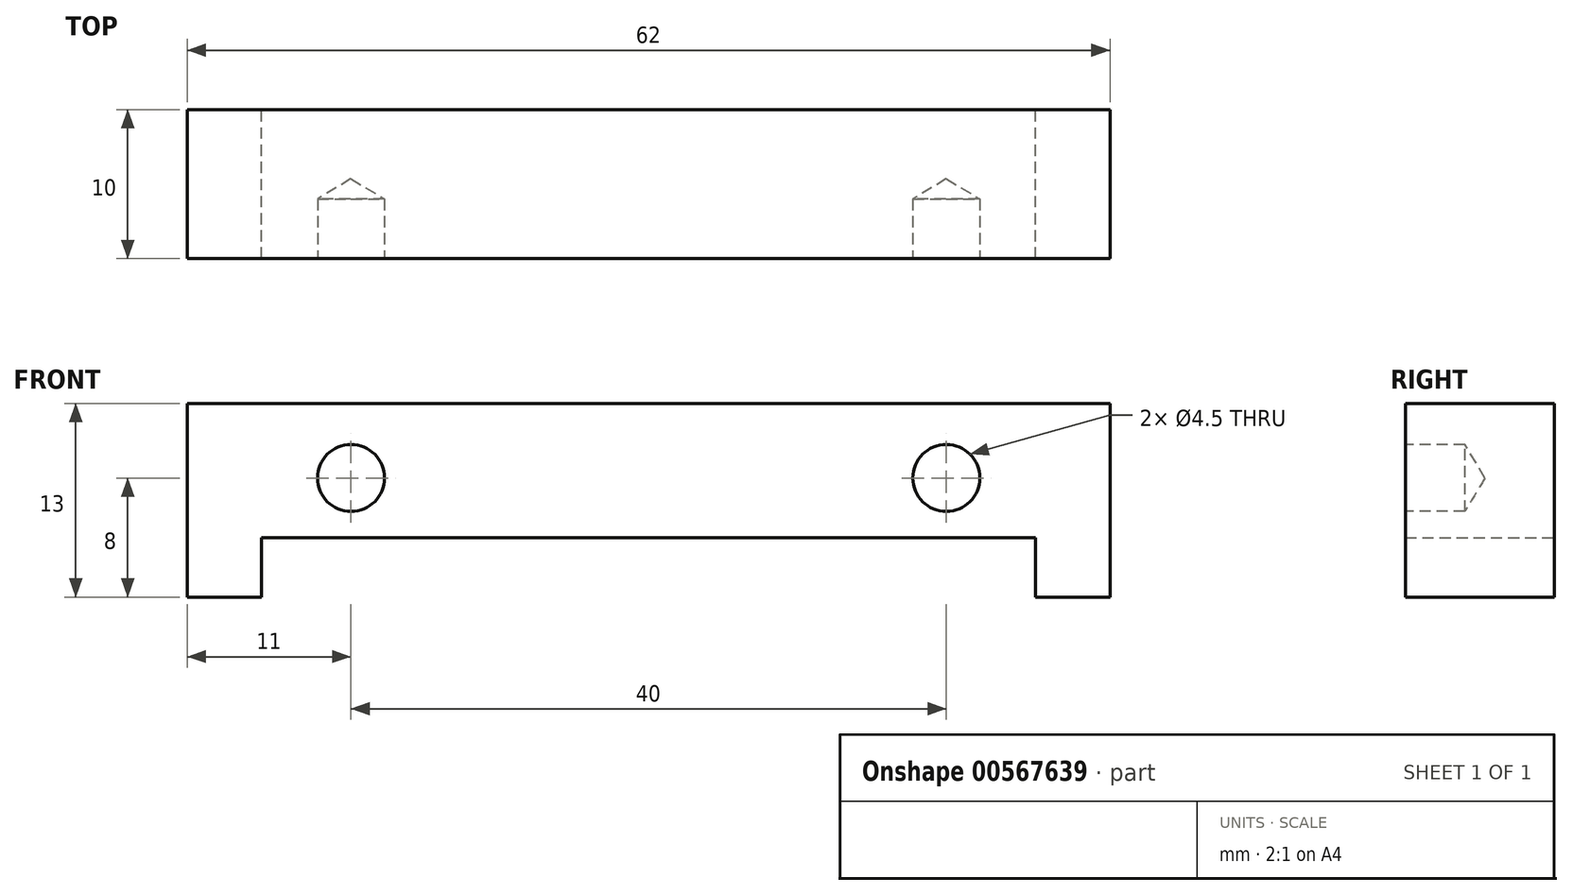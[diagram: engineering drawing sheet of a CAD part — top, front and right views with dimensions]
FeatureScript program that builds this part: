
annotation { "Feature Type Name" : "Feature", "Feature Type Description" : "" }
export const myFeature = defineFeature(function(context is Context, id is Id, definition is map)
    precondition{}
    {
        {
            var Q0;
            Q0=qCreatedBy(makeId("Front.planeOp"),FACE);
            var sketch = newSketch(context, id + "F0", { "sketchPlane" : qUnion([Q0])});
            skLineSegment(sketch, "E0", {"start": v(0, 0) * mm, "end": v(0, 13) * mm});
            skLineSegment(sketch, "E1", {"start": v(0, 13) * mm, "end": v(62, 13) * mm});
            skLineSegment(sketch, "E2", {"start": v(62, 13) * mm, "end": v(62, 0) * mm});
            skLineSegment(sketch, "E3", {"start": v(62, 0) * mm, "end": v(57, 0) * mm});
            skLineSegment(sketch, "E4", {"start": v(57, 0) * mm, "end": v(57, 4) * mm});
            skLineSegment(sketch, "E5", {"start": v(57, 4) * mm, "end": v(5, 4) * mm});
            skLineSegment(sketch, "E6", {"start": v(5, 4) * mm, "end": v(5, 0) * mm});
            skLineSegment(sketch, "E7", {"start": v(5, 0) * mm, "end": v(0, 0) * mm});
            skSolve(sketch);
        }
        {
            var Q0;
            Q0=makeQuery(id+"F0.imprint","IMPRINT",FACE,{"disambiguationData":[TD([[makeQuery(id+"F0.imprint","IMPRINT",EDGE,{"derivedFrom":sQuery(id+"F0.wireOp",EDGE,"E0")}),-1.0]])]});
            extrude(context, id + "F1", {"entities" : qUnion([Q0]), "depth" : 10 * mm, "offsetDistance" : 25 * mm});
        }
        {
            var Q0;
            Q0=makeQuery(id+"F1.opExtrude","CAP_FACE",FACE,{"disambiguationData":[OSD([sQuery(id+"F0.wireOp",EDGE,"E0"),sQuery(id+"F0.wireOp",EDGE,"E1"),sQuery(id+"F0.wireOp",EDGE,"E2"),sQuery(id+"F0.wireOp",EDGE,"E3"),sQuery(id+"F0.wireOp",EDGE,"E4"),sQuery(id+"F0.wireOp",EDGE,"E5"),sQuery(id+"F0.wireOp",EDGE,"E6"),sQuery(id+"F0.wireOp",EDGE,"E7")])],"isStart":false});
            var sketch = newSketch(context, id + "F2", { "sketchPlane" : qUnion([Q0])});
            skLineSegment(sketch, "E8", {"start": v(0, 8) * mm, "end": v(11, 8) * mm});
            skLineSegment(sketch, "E9", {"start": v(11, 8) * mm, "end": v(11, 13) * mm});
            skLineSegment(sketch, "E10", {"start": v(62, 8) * mm, "end": v(51, 8) * mm});
            skLineSegment(sketch, "E11", {"start": v(51, 8) * mm, "end": v(51, 13) * mm});
            skSolve(sketch);
        }
        {
            var Q0;
            Q0=sQuery(id+"F2.wireOp",VERTEX,"E9.start");
            var Q1;
            Q1=sQuery(id+"F2.wireOp",VERTEX,"E11.start");
            var Q2;
            Q2=makeQuery(id+"F1.opExtrude","SWEPT_BODY",BODY,{"disambiguationData":[OSD([sQuery(id+"F0.wireOp",EDGE,"E0"),sQuery(id+"F0.wireOp",EDGE,"E1"),sQuery(id+"F0.wireOp",EDGE,"E2"),sQuery(id+"F0.wireOp",EDGE,"E3"),sQuery(id+"F0.wireOp",EDGE,"E4"),sQuery(id+"F0.wireOp",EDGE,"E5"),sQuery(id+"F0.wireOp",EDGE,"E6"),sQuery(id+"F0.wireOp",EDGE,"E7")])]});
            hole(context, id + "F3", {"style" : HoleStyle.SIMPLE, "endStyle" : HoleEndStyle.BLIND, "standardTappedOrClearance" : lookupTablePath({ "standard" : "ISO", "size" : "4.5", "type" : "Drilled" }), "standardBlindInLast" : lookupTablePath({ "standard" : "ISO", "size" : "4.5", "type" : "Drilled" }), "holeDiameter" : 4.5 * mm, "holeDepth" : 4 * mm, "isTappedThrough" : true, "tappedDepth" : 12 * mm, "tapClearance" : 3, "locations" : qUnion([Q0, Q1]), "scope" : qUnion([Q2])});
        }
    });
